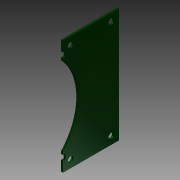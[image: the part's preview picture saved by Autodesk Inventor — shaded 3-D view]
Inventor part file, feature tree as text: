
AUTODESK INVENTOR PART (.ipt)
format: ipt  version: 2013 (Build 170138000, 138)  size: 118,784 bytes
history: native  units: in
note: dims shown in document units (in); Inventor stores cm internally (conversion verified against a paired STEP export)
features: extrude x1, sketch x1
ambient origin geometry x8: Origin, YZ Plane, XZ Plane, XY Plane, X Axis, Y Axis, Z Axis, Center Point
bodies: Solid1 (feature_tree)
feature tree (2):
  extrude  "Extrusion1"  Depth=1.1in
  sketch  "Sketch1"  dims[d0=2.25in d1=1.1in d2=1.1in d3=0.5841in d4=1.1471in d5=0.1102in d6=0.15in d7=0.15in d8=0.2in d9=0.05in d10=0.1in d11=0.05in d12=0.0394in d13=0.0in d14=0.1102in d15=0.8in d16=1.9458in d17=0.35in d18=1.95in]
